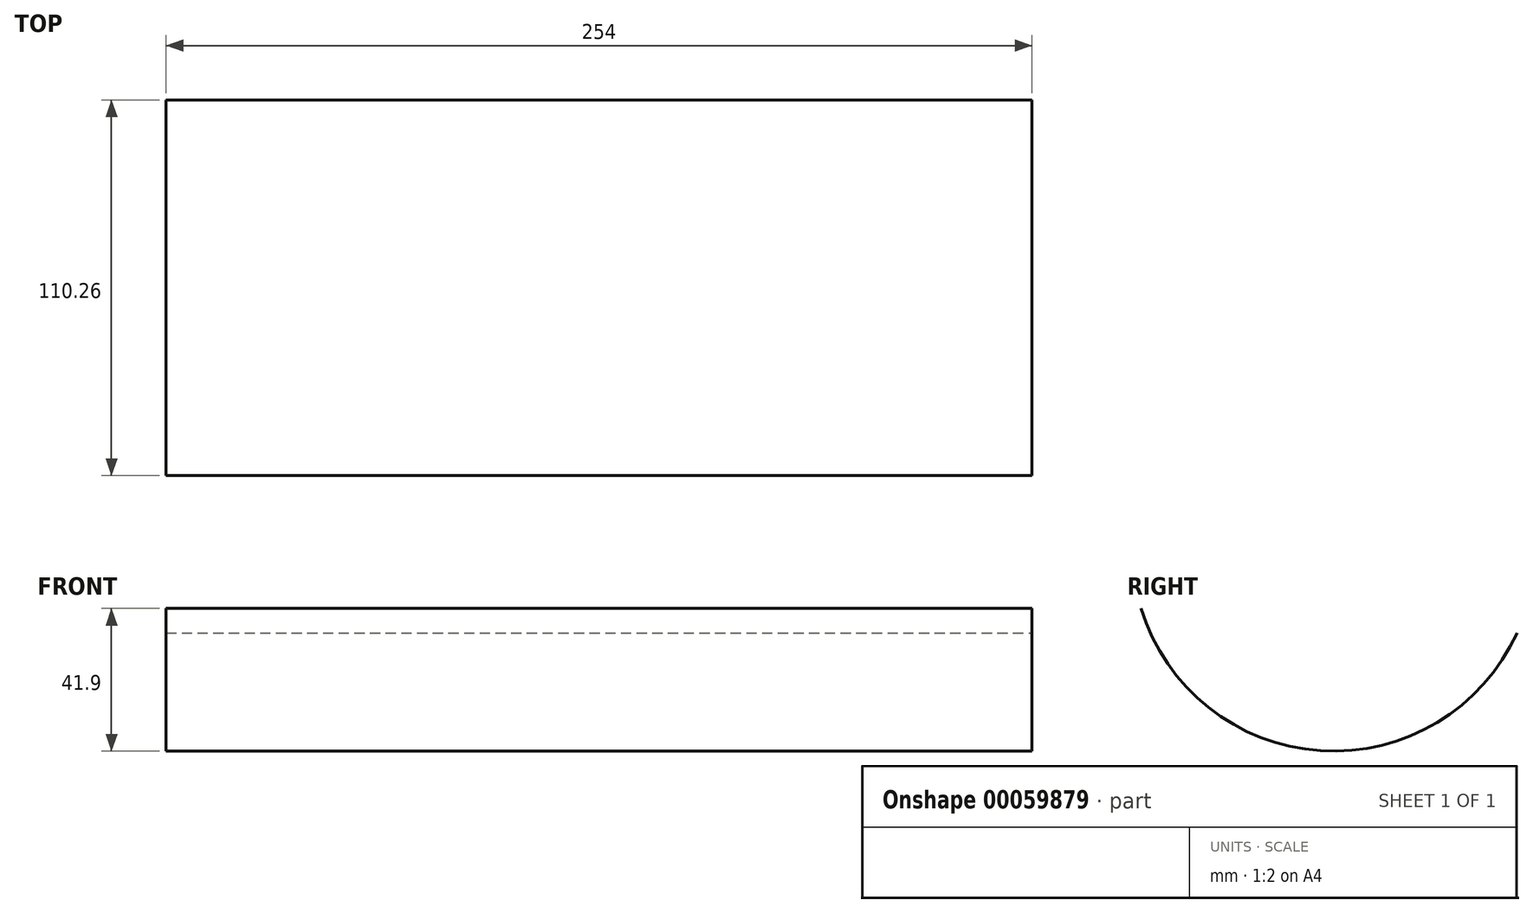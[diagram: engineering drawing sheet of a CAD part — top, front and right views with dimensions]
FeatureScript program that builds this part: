
annotation { "Feature Type Name" : "Feature", "Feature Type Description" : "" }
export const myFeature = defineFeature(function(context is Context, id is Id, definition is map)
    precondition{}
    {
        {
            var Q0;
            Q0=qCreatedBy(makeId("Right.planeOp"),FACE);
            var sketch = newSketch(context, id + "F0", { "sketchPlane" : qUnion([Q0])});
            skArc(sketch, "E0", {"start": v(-54.53, 41.87) * mm, "mid": v(-1.88, 0.1) * mm, "end": v(55.73, 34.72) * mm});
            skSolve(sketch);
        }
        {
            var Q0;
            Q0=sQuery(id+"F0.wireOp",EDGE,"E0");
            extrude(context, id + "F1", {"bodyType" : ToolBodyType.SURFACE, "surfaceEntities" : qUnion([Q0]), "depth" : 254 * mm});
        }
    });
